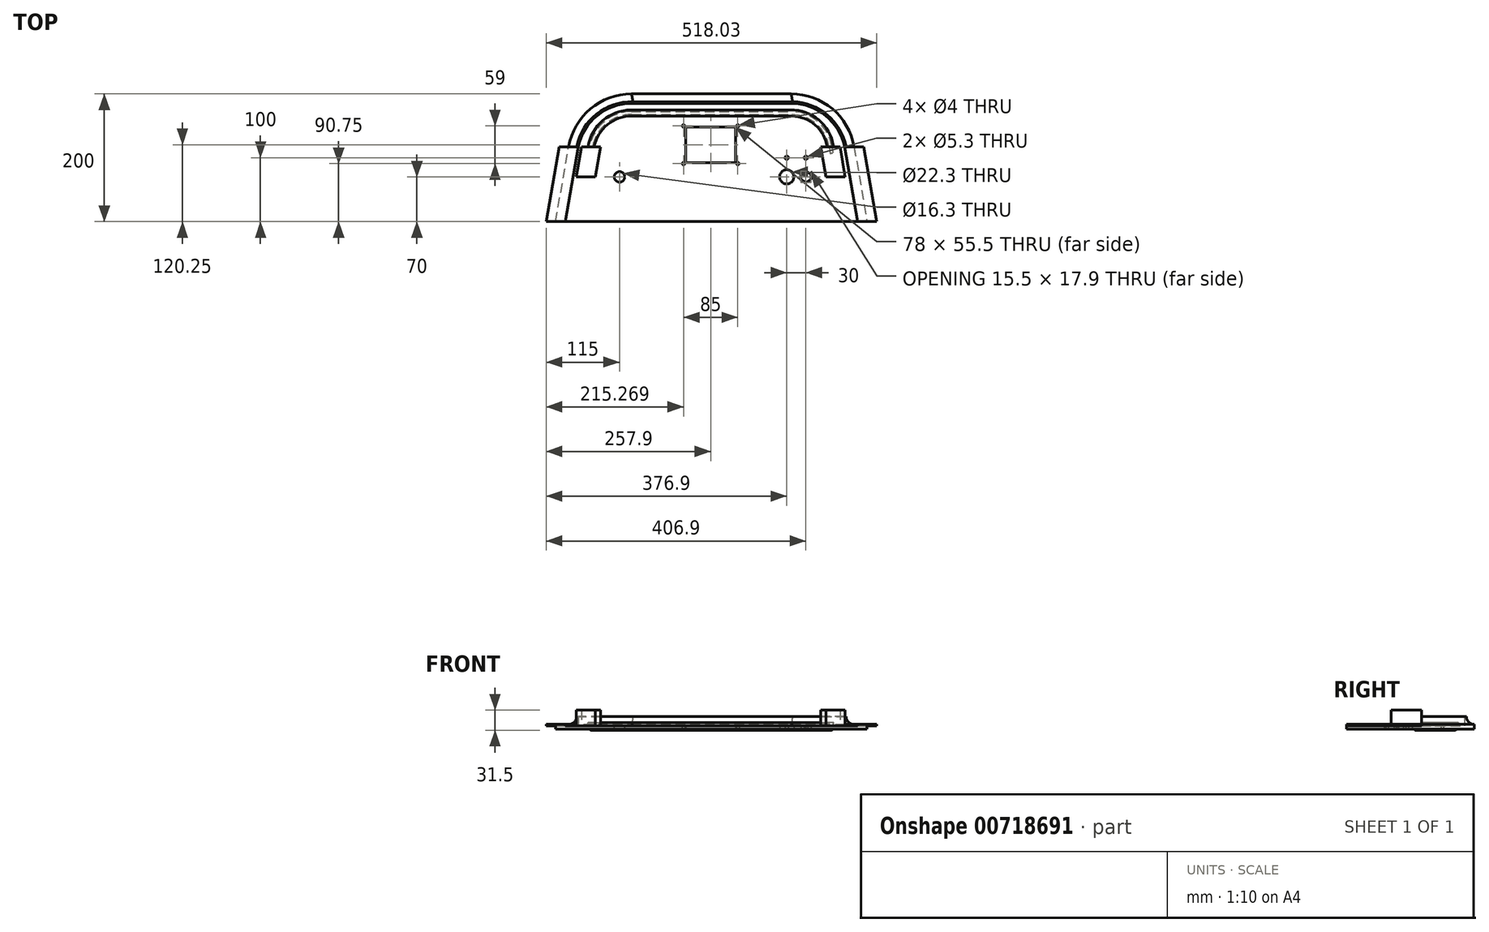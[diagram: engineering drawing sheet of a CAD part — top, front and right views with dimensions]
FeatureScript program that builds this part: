
annotation { "Feature Type Name" : "Feature", "Feature Type Description" : "" }
export const myFeature = defineFeature(function(context is Context, id is Id, definition is map)
    precondition{}
    {
        {
            var Q0;
            Q0=qCreatedBy(makeId("Top.planeOp"),FACE);
            var sketch = newSketch(context, id + "F0", { "sketchPlane" : qUnion([Q0])});
            skLineSegment(sketch, "E0", {"start": v(0, 0) * mm, "end": v(20.38, 117.14) * mm});
            skArc(sketch, "E1", {"start": v(118.9, 200) * mm, "mid": v(54.54, 176.53) * mm, "end": v(20.38, 117.14) * mm});
            skLineSegment(sketch, "E2", {"start": v(118.9, 200) * mm, "end": v(368.9, 200) * mm});
            skArc(sketch, "E3", {"start": v(467.42, 117.14) * mm, "mid": v(433.27, 176.53) * mm, "end": v(368.9, 200) * mm});
            skLineSegment(sketch, "E4", {"start": v(467.42, 117.14) * mm, "end": v(487.8, 0) * mm});
            skLineSegment(sketch, "E5", {"start": v(0, 0) * mm, "end": v(487.8, 0) * mm});
            skPoint(sketch, "E6.start.orphan", {"position": v(0, 0) * mm});
            skPoint(sketch, "E7.orphan", {"position": v(487.8, 0) * mm});
            skSolve(sketch);
        }
        {
            var Q0;
            Q0=makeQuery(id+"F0.imprint","IMPRINT",FACE,{"disambiguationData":[TD([[makeQuery(id+"F0.imprint","IMPRINT",EDGE,{"derivedFrom":sQuery(id+"F0.wireOp",EDGE,"E0")}),-1.0]])]});
            extrude(context, id + "F1", {"entities" : qUnion([Q0]), "oppositeDirection" : true, "depth" : 5 * mm, "offsetDistance" : 25 * mm});
        }
        {
            var Q0;
            Q0=makeQuery(id+"F1.opExtrude","CAP_FACE",FACE,{"disambiguationData":[OSD([sQuery(id+"F0.wireOp",EDGE,"E0"),sQuery(id+"F0.wireOp",EDGE,"E1"),sQuery(id+"F0.wireOp",EDGE,"E2"),sQuery(id+"F0.wireOp",EDGE,"E3"),sQuery(id+"F0.wireOp",EDGE,"E4"),sQuery(id+"F0.wireOp",EDGE,"E5")])],"isStart":true});
            var sketch = newSketch(context, id + "F2", { "sketchPlane" : qUnion([Q0])});
            skArc(sketch, "E8.0", {"start": v(118.9, 200) * mm, "mid": v(54.54, 176.53) * mm, "end": v(20.38, 117.14) * mm});
            skLineSegment(sketch, "E9.0", {"start": v(118.9, 200) * mm, "end": v(368.9, 200) * mm});
            skArc(sketch, "E10.0", {"start": v(467.42, 117.14) * mm, "mid": v(433.27, 176.53) * mm, "end": v(368.9, 200) * mm});
            skLineSegment(sketch, "E11", {"start": v(20.38, 117.14) * mm, "end": v(35.38, 117.14) * mm});
            skLineSegment(sketch, "E12", {"start": v(118.9, 185) * mm, "end": v(368.9, 185) * mm});
            skLineSegment(sketch, "E13", {"start": v(452.42, 117.14) * mm, "end": v(467.42, 117.14) * mm});
            skArc(sketch, "E14", {"start": v(118.9, 185) * mm, "mid": v(65.1, 165.9) * mm, "end": v(35.38, 117.14) * mm});
            skArc(sketch, "E15", {"start": v(452.42, 117.14) * mm, "mid": v(422.7, 165.9) * mm, "end": v(368.9, 185) * mm});
            skSolve(sketch);
        }
        {
            var Q0;
            Q0=makeQuery(id+"F2.imprint","IMPRINT",FACE,{"disambiguationData":[TD([[makeQuery(id+"F2.imprint","IMPRINT",EDGE,{"derivedFrom":sQuery(id+"F2.wireOp",EDGE,"E8.0")}),1.0]])]});
            extrude(context, id + "F3", {"entities" : qUnion([Q0]), "operationType" : NewBodyOperationType.ADD, "depth" : 15 * mm, "offsetDistance" : 25 * mm});
        }
        {
            var Q0;
            Q0=makeQuery(id+"F3.opExtrude","SWEPT_FACE",FACE,{"disambiguationData":[OSD([sQuery(id+"F2.wireOp",EDGE,"E11")])]});
            var sketch = newSketch(context, id + "F4", { "sketchPlane" : qUnion([Q0])});
            skCircle(sketch, "E16", {"center": v(20.38, 15) * mm, "radius": 12.5 * mm});
            skSolve(sketch);
        }
        {
            var Q0;
            Q0=makeQuery(id+"F3.opExtrude","CAP_FACE",FACE,{"disambiguationData":[OSD([sQuery(id+"F2.wireOp",EDGE,"E8.0"),sQuery(id+"F2.wireOp",EDGE,"E9.0"),sQuery(id+"F2.wireOp",EDGE,"E10.0"),sQuery(id+"F2.wireOp",EDGE,"E11"),sQuery(id+"F2.wireOp",EDGE,"E12"),sQuery(id+"F2.wireOp",EDGE,"E13"),sQuery(id+"F2.wireOp",EDGE,"E14"),sQuery(id+"F2.wireOp",EDGE,"E15")])],"isStart":false});
            var sketch = newSketch(context, id + "F5", { "sketchPlane" : qUnion([Q0])});
            skArc(sketch, "E17.0", {"start": v(118.9, 200) * mm, "mid": v(54.54, 176.53) * mm, "end": v(20.38, 117.14) * mm});
            skLineSegment(sketch, "E18.0", {"start": v(118.9, 200) * mm, "end": v(368.9, 200) * mm});
            skArc(sketch, "E19.0", {"start": v(467.42, 117.14) * mm, "mid": v(433.27, 176.53) * mm, "end": v(368.9, 200) * mm});
            skSolve(sketch);
        }
        {
            var Q0;
            {var subQ0=sQuery(id+"F4.wireOp",EDGE,"E16");var subQ1=sQuery(id+"F2.wireOp",EDGE,"E11");var subQ4=makeQuery(id+"F3.opExtrude","CAP_EDGE",EDGE,{"disambiguationData":[OSD([subQ1])],"isStart":false});var subQ5=makeQuery(id+"F4.imprint","INTERSECT",VERTEX,{"derivedFrom":[subQ4,subQ0]});Q0=makeQuery(id+"F4.imprint","IMPRINT",FACE,{"disambiguationData":[TD([[makeQuery(id+"F4.imprint","IMPRINT",EDGE,{"disambiguationData":[TD([[subQ5,1.0]])],"derivedFrom":subQ0}),1.0]])]});}
            var Q1;
            Q1 = qConstructionFilter(qBodyType(qCreatedBy(id + "F5" ,EDGE), BodyType.WIRE), ConstructionObject.NO);
            sweep(context, id + "F6", {"operationType" : NewBodyOperationType.REMOVE, "profiles" : qUnion([Q0]), "path" : qUnion([Q1])});
        }
        {
            var Q0;
            Q0=makeQuery(id+"F1.opExtrude","CAP_FACE",FACE,{"disambiguationData":[OSD([sQuery(id+"F0.wireOp",EDGE,"E0"),sQuery(id+"F0.wireOp",EDGE,"E1"),sQuery(id+"F0.wireOp",EDGE,"E2"),sQuery(id+"F0.wireOp",EDGE,"E3"),sQuery(id+"F0.wireOp",EDGE,"E4"),sQuery(id+"F0.wireOp",EDGE,"E5")])],"isStart":true});
            var sketch = newSketch(context, id + "F7", { "sketchPlane" : qUnion([Q0])});
            skLineSegment(sketch, "E20", {"start": v(15, 0) * mm, "end": v(35.38, 117.14) * mm});
            skLineSegment(sketch, "E21", {"start": v(35.38, 117.14) * mm, "end": v(5.38, 117.14) * mm});
            skLineSegment(sketch, "E22", {"start": v(5.38, 117.14) * mm, "end": v(-15, 0) * mm});
            skLineSegment(sketch, "E23", {"start": v(-15, 0) * mm, "end": v(15, 0) * mm});
            skLineSegment(sketch, "E24", {"start": v(452.42, 117.14) * mm, "end": v(482.42, 117.14) * mm});
            skLineSegment(sketch, "E25", {"start": v(482.42, 117.14) * mm, "end": v(503.03, 0) * mm});
            skLineSegment(sketch, "E26", {"start": v(503.03, 0) * mm, "end": v(473.03, 0) * mm});
            skLineSegment(sketch, "E27", {"start": v(473.03, 0) * mm, "end": v(452.42, 117.14) * mm});
            skSolve(sketch);
        }
        {
            var Q0;
            {var subQ2=sQuery(id+"F7.wireOp",EDGE,"E22");Q0=makeQuery(id+"F7.imprint","IMPRINT",FACE,{"disambiguationData":[TD([[makeQuery(id+"F7.imprint","IMPRINT",EDGE,{"derivedFrom":subQ2}),1.0]])]});}
            var Q1;
            {var subQ0=sQuery(id+"F7.wireOp",EDGE,"E20");Q1=makeQuery(id+"F7.imprint","IMPRINT",FACE,{"disambiguationData":[TD([[makeQuery(id+"F7.imprint","IMPRINT",EDGE,{"derivedFrom":subQ0}),1.0]])]});}
            var Q2;
            {var subQ2=sQuery(id+"F7.wireOp",EDGE,"E27");Q2=makeQuery(id+"F7.imprint","IMPRINT",FACE,{"disambiguationData":[TD([[makeQuery(id+"F7.imprint","IMPRINT",EDGE,{"derivedFrom":subQ2}),-1.0]])]});}
            var Q3;
            {var subQ2=sQuery(id+"F7.wireOp",EDGE,"E25");Q3=makeQuery(id+"F7.imprint","IMPRINT",FACE,{"disambiguationData":[TD([[makeQuery(id+"F7.imprint","IMPRINT",EDGE,{"derivedFrom":subQ2}),-1.0]])]});}
            extrude(context, id + "F8", {"entities" : qUnion([Q0, Q1, Q2, Q3]), "operationType" : NewBodyOperationType.ADD, "depth" : 2.5 * mm, "offsetDistance" : 25 * mm});
        }
        {
            var Q0;
            Q0=makeQuery(id+"F1.opExtrude","CAP_FACE",FACE,{"disambiguationData":[OSD([sQuery(id+"F0.wireOp",EDGE,"E0"),sQuery(id+"F0.wireOp",EDGE,"E1"),sQuery(id+"F0.wireOp",EDGE,"E2"),sQuery(id+"F0.wireOp",EDGE,"E3"),sQuery(id+"F0.wireOp",EDGE,"E4"),sQuery(id+"F0.wireOp",EDGE,"E5")])],"isStart":false});
            var sketch = newSketch(context, id + "F9", { "sketchPlane" : qUnion([Q0])});
            skLineSegment(sketch, "E28.bottom", {"start": v(203.9, -148) * mm, "end": v(281.9, -148) * mm});
            skLineSegment(sketch, "E28.top", {"start": v(203.9, -92.5) * mm, "end": v(281.9, -92.5) * mm});
            skLineSegment(sketch, "E28.left", {"start": v(203.9, -148) * mm, "end": v(203.9, -92.5) * mm});
            skLineSegment(sketch, "E28.right", {"start": v(281.9, -148) * mm, "end": v(281.9, -92.5) * mm});
            skCircle(sketch, "E29", {"center": v(200.27, -149.75) * mm, "radius": 2 * mm});
            skCircle(sketch, "E30", {"center": v(200.27, -90.75) * mm, "radius": 2 * mm});
            skCircle(sketch, "E31", {"center": v(285.27, -90.75) * mm, "radius": 2 * mm});
            skCircle(sketch, "E32", {"center": v(285.27, -149.75) * mm, "radius": 2 * mm});
            skSolve(sketch);
        }
        {
            var Q0;
            Q0 = qSketchRegion(id + "F9", true);
            extrude(context, id + "F10", {"entities" : qUnion([Q0]), "operationType" : NewBodyOperationType.REMOVE, "oppositeDirection" : true, "depth" : 25 * mm, "offsetDistance" : 25 * mm});
        }
        {
            var Q0;
            Q0=makeQuery(id+"F1.opExtrude","CAP_FACE",FACE,{"disambiguationData":[OSD([sQuery(id+"F0.wireOp",EDGE,"E0"),sQuery(id+"F0.wireOp",EDGE,"E1"),sQuery(id+"F0.wireOp",EDGE,"E2"),sQuery(id+"F0.wireOp",EDGE,"E3"),sQuery(id+"F0.wireOp",EDGE,"E4"),sQuery(id+"F0.wireOp",EDGE,"E5")])],"isStart":false});
            var sketch = newSketch(context, id + "F11", { "sketchPlane" : qUnion([Q0])});
            skCircle(sketch, "E33.cCircle", {"center": v(391.9, -70) * mm, "radius": 8.95 * mm, "construction": true});
            skLineSegment(sketch, "E33.0", {"start": v(399.65, -74.47) * mm, "end": v(391.9, -78.95) * mm});
            skLineSegment(sketch, "E33.1", {"start": v(391.9, -78.95) * mm, "end": v(384.15, -74.47) * mm});
            skLineSegment(sketch, "E33.2", {"start": v(384.15, -74.47) * mm, "end": v(384.15, -65.53) * mm});
            skLineSegment(sketch, "E33.3", {"start": v(384.15, -65.53) * mm, "end": v(391.9, -61.05) * mm});
            skLineSegment(sketch, "E33.4", {"start": v(391.9, -61.05) * mm, "end": v(399.65, -65.53) * mm});
            skLineSegment(sketch, "E33.5", {"start": v(399.65, -65.53) * mm, "end": v(399.65, -74.47) * mm});
            skCircle(sketch, "E34", {"center": v(361.9, -70) * mm, "radius": 11.15 * mm});
            skCircle(sketch, "E35", {"center": v(361.9, -100) * mm, "radius": 2.65 * mm});
            skCircle(sketch, "E36", {"center": v(391.9, -100) * mm, "radius": 2.65 * mm});
            skSolve(sketch);
        }
        {
            var Q0;
            Q0 = qSketchRegion(id + "F11", true);
            extrude(context, id + "F12", {"entities" : qUnion([Q0]), "operationType" : NewBodyOperationType.REMOVE, "oppositeDirection" : true, "depth" : 25 * mm, "offsetDistance" : 25 * mm});
        }
        {
            var Q0;
            Q0=makeQuery(id+"F1.opExtrude","CAP_FACE",FACE,{"disambiguationData":[OSD([sQuery(id+"F0.wireOp",EDGE,"E0"),sQuery(id+"F0.wireOp",EDGE,"E1"),sQuery(id+"F0.wireOp",EDGE,"E2"),sQuery(id+"F0.wireOp",EDGE,"E3"),sQuery(id+"F0.wireOp",EDGE,"E4"),sQuery(id+"F0.wireOp",EDGE,"E5")])],"isStart":true});
            var sketch = newSketch(context, id + "F13", { "sketchPlane" : qUnion([Q0])});
            skCircle(sketch, "E37", {"center": v(100, 70) * mm, "radius": 8.15 * mm});
            skSolve(sketch);
        }
        {
            var Q0;
            Q0=makeQuery(id+"F13.imprint","IMPRINT",FACE,{"disambiguationData":[TD([[makeQuery(id+"F13.imprint","IMPRINT",EDGE,{"derivedFrom":sQuery(id+"F13.wireOp",EDGE,"E37")}),1.0]])]});
            extrude(context, id + "F14", {"entities" : qUnion([Q0]), "operationType" : NewBodyOperationType.REMOVE, "oppositeDirection" : true, "depth" : 25 * mm, "offsetDistance" : 25 * mm});
        }
        {
            var Q0;
            Q0=makeQuery(id+"F1.opExtrude","CAP_FACE",FACE,{"disambiguationData":[OSD([sQuery(id+"F0.wireOp",EDGE,"E0"),sQuery(id+"F0.wireOp",EDGE,"E1"),sQuery(id+"F0.wireOp",EDGE,"E2"),sQuery(id+"F0.wireOp",EDGE,"E3"),sQuery(id+"F0.wireOp",EDGE,"E4"),sQuery(id+"F0.wireOp",EDGE,"E5")])],"isStart":true});
            var sketch = newSketch(context, id + "F15", { "sketchPlane" : qUnion([Q0])});
            skLineSegment(sketch, "E38", {"start": v(32.25, 70) * mm, "end": v(40.46, 117.14) * mm});
            skLineSegment(sketch, "E39", {"start": v(40.46, 117.14) * mm, "end": v(70.46, 117.14) * mm});
            skLineSegment(sketch, "E40", {"start": v(70.46, 117.14) * mm, "end": v(62.25, 70) * mm});
            skLineSegment(sketch, "E41", {"start": v(62.25, 70) * mm, "end": v(32.25, 70) * mm});
            skLineSegment(sketch, "E42", {"start": v(242.9, 148) * mm, "end": v(242.9, 92.5) * mm});
            skLineSegment(sketch, "E43.MirrorCS", {"start": v(423.55, 70) * mm, "end": v(453.55, 70) * mm});
            skLineSegment(sketch, "E44.MirrorCS", {"start": v(415.34, 117.14) * mm, "end": v(423.55, 70) * mm});
            skLineSegment(sketch, "E45.MirrorCS", {"start": v(445.34, 117.14) * mm, "end": v(415.34, 117.14) * mm});
            skLineSegment(sketch, "E46.MirrorCS", {"start": v(453.55, 70) * mm, "end": v(445.34, 117.14) * mm});
            skSolve(sketch);
        }
        {
            var Q0;
            Q0 = qSketchRegion(id + "F15", true);
            extrude(context, id + "F16", {"entities" : qUnion([Q0]), "operationType" : NewBodyOperationType.ADD, "depth" : 25 * mm, "offsetDistance" : 25 * mm});
        }
        {
            var Q0;
            Q0=makeQuery(id+"F16.opExtrude","SWEPT_FACE",FACE,{"disambiguationData":[OSD([sQuery(id+"F15.wireOp",EDGE,"E39")])]});
            var sketch = newSketch(context, id + "F17", { "sketchPlane" : qUnion([Q0])});
            skLineSegment(sketch, "E47.bottom", {"start": v(-60.46, 0) * mm, "end": v(-50.46, 0) * mm});
            skLineSegment(sketch, "E47.top", {"start": v(-60.46, 5) * mm, "end": v(-50.46, 5) * mm});
            skLineSegment(sketch, "E47.left", {"start": v(-60.46, 0) * mm, "end": v(-60.46, 5) * mm});
            skLineSegment(sketch, "E47.right", {"start": v(-50.46, 0) * mm, "end": v(-50.46, 5) * mm});
            skCircle(sketch, "E48", {"center": v(-55.46, -4) * mm, "radius": 2.5 * mm});
            skPoint(sketch, "E48.centerSnap0", {"position": v(-55.46, 5) * mm});
            skSolve(sketch);
        }
        {
            var Q0;
            Q0=makeQuery(id+"F1.opExtrude","CAP_FACE",FACE,{"disambiguationData":[OSD([sQuery(id+"F0.wireOp",EDGE,"E0"),sQuery(id+"F0.wireOp",EDGE,"E1"),sQuery(id+"F0.wireOp",EDGE,"E2"),sQuery(id+"F0.wireOp",EDGE,"E3"),sQuery(id+"F0.wireOp",EDGE,"E4"),sQuery(id+"F0.wireOp",EDGE,"E5")])],"isStart":true});
            var sketch = newSketch(context, id + "F18", { "sketchPlane" : qUnion([Q0])});
            skArc(sketch, "E49", {"start": v(118.9, 170) * mm, "mid": v(77.61, 155.05) * mm, "end": v(55.46, 117.14) * mm});
            skArc(sketch, "E50", {"start": v(430.34, 117.14) * mm, "mid": v(409.43, 154.97) * mm, "end": v(368.9, 170) * mm});
            skLineSegment(sketch, "E51", {"start": v(118.9, 170) * mm, "end": v(368.9, 170) * mm});
            skLineSegment(sketch, "E52", {"start": v(430.34, 117.14) * mm, "end": v(431.84, 107.25) * mm});
            skSolve(sketch);
        }
        {
            var Q0;
            Q0 = qSketchRegion(id + "F17", true);
            var Q1;
            Q1 = qConstructionFilter(qBodyType(qCreatedBy(id + "F18" ,EDGE), BodyType.WIRE), ConstructionObject.NO);
            sweep(context, id + "F19", {"operationType" : NewBodyOperationType.ADD, "profiles" : qUnion([Q0]), "path" : qUnion([Q1])});
        }
    });
